# Revit family: ICF
name_source: partatom
category: Оборудование
units: mm (PartAtom-declared; Revit-internal decimal feet)

## family parameters
Всегда вертикально = Да
Классификация = Нет
На основе рабочей плоскости = Нет
Общий = Нет
При загрузке вырезать с полостями = Нет
Размер круглого соединителя = Использовать диаметр
Тип детали = Нормальный
Точка принадлежности помещению = Нет

## types (24) — shared parameters
00_20_Manufacturer = Вентс
00_20_Name = Відцентровий імпульсний вентилятор
Casing Material = Металл, окрашенный, синий, матовый RAL 5007
Grid Material = Cover Grid Cross
Load Classification = HVAC
Maintenance zone material = <По категории>
Number of Fase = 3
Voltage = 400 В
Струм = 0 А
zero-valued in all types: Отметка по умолчанию

## per-type parameters (varying)
| type | A | A1 | A2 | B | C | L | L1 | Maximum Air Flow | Power | a | a1 | c1 | Вага | Двигатель | Решетка |
| ICF-50N-4 | 290 мм | 190 мм | 90 мм | 1355 мм | 935 мм | 180 мм | 410 мм | 1720.0 л/с | 1500 Вт | 43 мм | 24 мм | 219 мм | 96.00 кг | Двигатель : Двигатель_1.5 кВт | Решетка круглая : 50N |
| ICF-100N-4 | 330 мм | 230 мм | 130 мм | 1605 мм | 1105 мм | 230 мм | 510 мм | 2830.0 л/с | 3000 Вт | 63 мм | 37 мм | 261 мм | 138.00 кг | Двигатель : Двигатель_3 кВт | Решетка круглая : 100N |
| ICF-85N-4 | 330 мм | 230 мм | 130 мм | 1605 мм | 1105 мм | 230 мм | 510 мм | 2700.0 л/с | 2200 Вт | 63 мм | 37 мм | 261 мм | 136.00 кг | Двигатель : Двигатель_2.2 кВт | Решетка круглая : 85N |
| ICF-50N-4-300/2 | 290 мм | 190 мм | 90 мм | 1355 мм | 935 мм | 180 мм | 410 мм | 1720.0 л/с | 1500 Вт | 43 мм | 24 мм | 219 мм | 96.00 кг | Двигатель : Двигатель_1.5 кВт | Решетка круглая : 50N |
| ICF-50N-4-400/2 | 290 мм | 190 мм | 90 мм | 1355 мм | 935 мм | 180 мм | 410 мм | 1720.0 л/с | 1500 Вт | 43 мм | 24 мм | 219 мм | 96.00 кг | Двигатель : Двигатель_1.5 кВт | Решетка круглая : 50N |
| ICF-50N-4/6 | 290 мм | 190 мм | 90 мм | 1355 мм | 935 мм | 180 мм | 410 мм | 1720.0 л/с | 1500 Вт | 43 мм | 24 мм | 219 мм | 96.00 кг | Двигатель : Двигатель_1.5 кВт | Решетка круглая : 50N |
| ICF-50N-4/6-300/2 | 290 мм | 190 мм | 90 мм | 1355 мм | 935 мм | 180 мм | 410 мм | 1720.0 л/с | 1500 Вт | 43 мм | 24 мм | 219 мм | 96.00 кг | Двигатель : Двигатель_1.5 кВт | Решетка круглая : 50N |
| ICF-50N-4/6-400/2 | 290 мм | 190 мм | 90 мм | 1355 мм | 935 мм | 180 мм | 410 мм | 1720.0 л/с | 1500 Вт | 43 мм | 24 мм | 219 мм | 96.00 кг | Двигатель : Двигатель_1.5 кВт | Решетка круглая : 50N |
| ICF-50N-4/8 | 290 мм | 190 мм | 90 мм | 1355 мм | 935 мм | 180 мм | 410 мм | 1720.0 л/с | 1600 Вт | 43 мм | 24 мм | 219 мм | 96.00 кг | Двигатель : Двигатель_1.6 кВт | Решетка круглая : 50N |
| ICF-50N-4/8-300/2 | 290 мм | 190 мм | 90 мм | 1355 мм | 935 мм | 180 мм | 410 мм | 1720.0 л/с | 1600 Вт | 43 мм | 24 мм | 219 мм | 96.00 кг | Двигатель : Двигатель_1.6 кВт | Решетка круглая : 50N |
| ICF-50N-4/8-400/2 | 290 мм | 190 мм | 90 мм | 1355 мм | 935 мм | 180 мм | 410 мм | 1720.0 л/с | 1600 Вт | 43 мм | 24 мм | 219 мм | 96.00 кг | Двигатель : Двигатель_1.6 кВт | Решетка круглая : 50N |
| ICF-85N-4-300/2 | 330 мм | 230 мм | 130 мм | 1605 мм | 1105 мм | 230 мм | 510 мм | 2700.0 л/с | 2200 Вт | 63 мм | 37 мм | 261 мм | 136.00 кг | Двигатель : Двигатель_2.2 кВт | Решетка круглая : 85N |
| ICF-85N-4-400/2 | 330 мм | 230 мм | 130 мм | 1605 мм | 1105 мм | 230 мм | 510 мм | 2700.0 л/с | 2200 Вт | 63 мм | 37 мм | 261 мм | 136.00 кг | Двигатель : Двигатель_2.2 кВт | Решетка круглая : 85N |
| ICF-85N-4/6 | 330 мм | 230 мм | 130 мм | 1605 мм | 1105 мм | 230 мм | 510 мм | 2700.0 л/с | 2200 Вт | 63 мм | 37 мм | 261 мм | 136.00 кг | Двигатель : Двигатель_2.2 кВт | Решетка круглая : 85N |
| ICF-85N-4/6-300/2 | 330 мм | 230 мм | 130 мм | 1605 мм | 1105 мм | 230 мм | 510 мм | 2700.0 л/с | 2200 Вт | 63 мм | 37 мм | 261 мм | 136.00 кг | Двигатель : Двигатель_2.2 кВт | Решетка круглая : 85N |
| ICF-85N-4/6-400/2 | 330 мм | 230 мм | 130 мм | 1605 мм | 1105 мм | 230 мм | 510 мм | 2700.0 л/с | 2200 Вт | 63 мм | 37 мм | 261 мм | 136.00 кг | Двигатель : Двигатель_2.2 кВт | Решетка круглая : 85N |
| ICF-85N-4/8 | 330 мм | 230 мм | 130 мм | 1605 мм | 1105 мм | 230 мм | 510 мм | 2700.0 л/с | 2200 Вт | 63 мм | 37 мм | 261 мм | 136.00 кг | Двигатель : Двигатель_2.2 кВт | Решетка круглая : 85N |
| ICF-85N-4/8-300/2 | 330 мм | 230 мм | 130 мм | 1605 мм | 1105 мм | 230 мм | 510 мм | 2700.0 л/с | 2200 Вт | 63 мм | 37 мм | 261 мм | 136.00 кг | Двигатель : Двигатель_2.2 кВт | Решетка круглая : 85N |
| ICF-85N-4/8-400/2 | 330 мм | 230 мм | 130 мм | 1605 мм | 1105 мм | 230 мм | 510 мм | 2700.0 л/с | 2200 Вт | 63 мм | 37 мм | 261 мм | 136.00 кг | Двигатель : Двигатель_2.2 кВт | Решетка круглая : 85N |
| ICF-100N-4-300/2 | 330 мм | 230 мм | 130 мм | 1605 мм | 1105 мм | 230 мм | 510 мм | 2830.0 л/с | 3000 Вт | 63 мм | 37 мм | 261 мм | 138.00 кг | Двигатель : Двигатель_3 кВт | Решетка круглая : 100N |
| ICF-100N-4-400/2 | 330 мм | 230 мм | 130 мм | 1605 мм | 1105 мм | 230 мм | 510 мм | 2830.0 л/с | 3000 Вт | 63 мм | 37 мм | 261 мм | 138.00 кг | Двигатель : Двигатель_3 кВт | Решетка круглая : 100N |
| ICF-100N-4/8 | 330 мм | 230 мм | 130 мм | 1605 мм | 1105 мм | 230 мм | 510 мм | 2830.0 л/с | 3000 Вт | 63 мм | 37 мм | 261 мм | 138.00 кг | Двигатель : Двигатель_3 кВт | Решетка круглая : 100N |
| ICF-100N-4/8-300/2 | 330 мм | 230 мм | 130 мм | 1605 мм | 1105 мм | 230 мм | 510 мм | 2830.0 л/с | 3000 Вт | 63 мм | 37 мм | 261 мм | 138.00 кг | Двигатель : Двигатель_3 кВт | Решетка круглая : 100N |
| ICF-100N-4/8-400/2 | 330 мм | 230 мм | 130 мм | 1605 мм | 1105 мм | 230 мм | 510 мм | 2830.0 л/с | 3000 Вт | 63 мм | 37 мм | 261 мм | 138.00 кг | Двигатель : Двигатель_3 кВт | Решетка круглая : 100N |

note: column(s) folded — value = type name in every type: 00_20_Type
